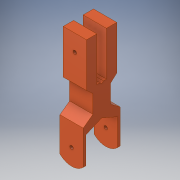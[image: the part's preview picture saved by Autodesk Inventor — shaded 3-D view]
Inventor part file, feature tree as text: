
AUTODESK INVENTOR PART (.ipt)
format: ipt  version: 2017 (Build 210142000, 142)  size: 155,648 bytes
history: native  units: in
note: dims shown in document units (in); Inventor stores cm internally (conversion verified against a paired STEP export)
features: sketch x3, extrude x3, plane x2, mirror x1
ambient origin geometry x8: Origin, YZ Plane, XZ Plane, XY Plane, X Axis, Y Axis, Z Axis, Center Point
bodies: Solid1 (feature_tree)
feature tree (9):
  sketch  "Sketch1"  dims[d3=0.2165in d6=0.7087in]
  plane  "Work Plane1"
  extrude  "Extrusion1"  Depth=0.7087in
  extrude  "Extrusion2"  Depth=0.5315in
  extrude  "Extrusion3"  Depth=1.4173in TaperAngle=0.0deg
  plane  "Work Plane3"
  mirror  "Mirror1"
  sketch  "Sketch3"  dims[d7=1.9882in d53=0.5315in]
  sketch  "Sketch5"  dims[d56=0.6299in d58=1.4173in d59=0.0in d60=0.1575in d61=0.0in d63=4.9213in d64=0.0in d65=0.2165in d66=1.1811in d67=0.0in]
